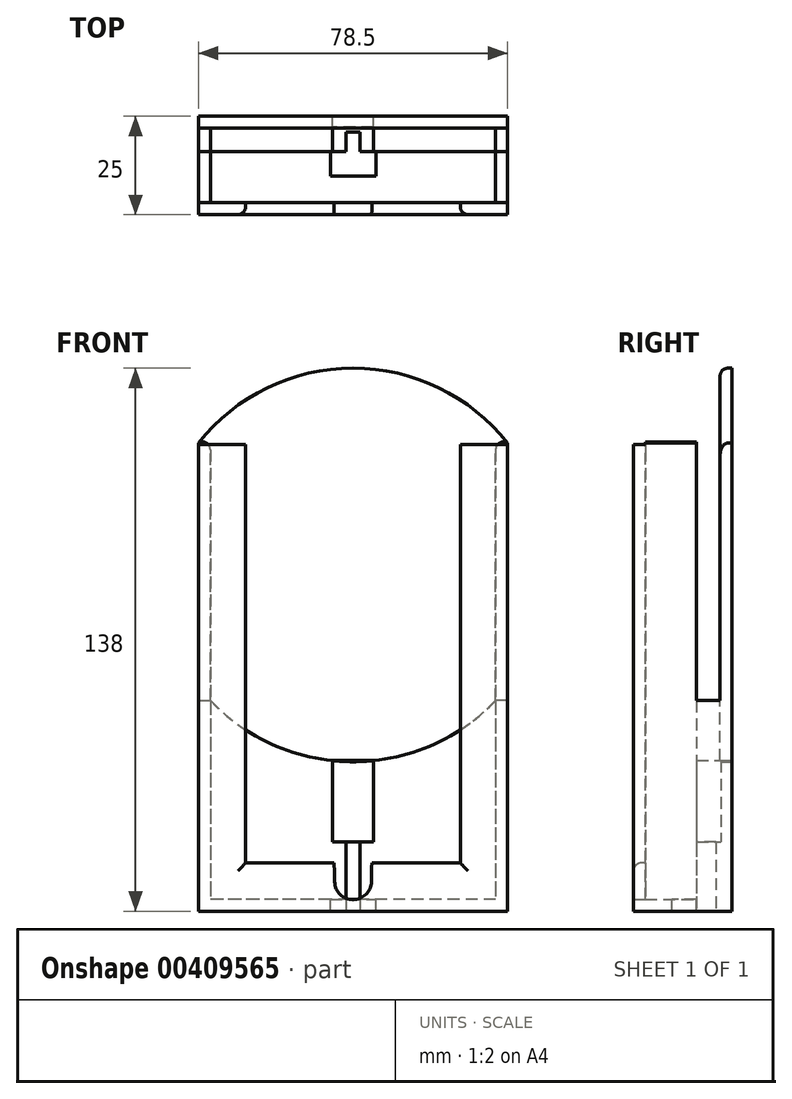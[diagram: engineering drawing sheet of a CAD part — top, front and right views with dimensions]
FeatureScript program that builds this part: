
annotation { "Feature Type Name" : "Feature", "Feature Type Description" : "" }
export const myFeature = defineFeature(function(context is Context, id is Id, definition is map)
    precondition{}
    {
        {
            var Q0;
            Q0=qCreatedBy(makeId("Front.planeOp"),FACE);
            var sketch = newSketch(context, id + "F0", { "sketchPlane" : qUnion([Q0])});
            skLineSegment(sketch, "E0.bottom", {"start": v(36.25, 70) * mm, "end": v(-36.25, 70) * mm});
            skLineSegment(sketch, "E0.top", {"start": v(36.25, -70) * mm, "end": v(-36.25, -70) * mm});
            skLineSegment(sketch, "E0.left", {"start": v(36.25, 70) * mm, "end": v(36.25, -70) * mm});
            skLineSegment(sketch, "E0.right", {"start": v(-36.25, 70) * mm, "end": v(-36.25, -70) * mm});
            skPoint(sketch, "E0.middle", {"position": v(0, 0) * mm});
            skLineSegment(sketch, "E1", {"start": v(0, -70) * mm, "end": v(0, -35) * mm, "construction": true});
            skLineSegment(sketch, "E2.bottom", {"start": v(39.25, 73) * mm, "end": v(-39.25, 73) * mm});
            skLineSegment(sketch, "E2.top", {"start": v(39.25, -73) * mm, "end": v(-39.25, -73) * mm});
            skLineSegment(sketch, "E2.left", {"start": v(39.25, 73) * mm, "end": v(39.25, -73) * mm});
            skLineSegment(sketch, "E2.right", {"start": v(-39.25, 73) * mm, "end": v(-39.25, -73) * mm});
            skLineSegment(sketch, "E3", {"start": v(-36.25, 70) * mm, "end": v(-36.25, 73) * mm});
            skLineSegment(sketch, "E4", {"start": v(36.25, 70) * mm, "end": v(36.25, 73) * mm});
            skLineSegment(sketch, "E5", {"start": v(0, -35) * mm, "end": v(0, 15) * mm, "construction": true});
            skCircle(sketch, "E6", {"center": v(0, 15) * mm, "radius": 50 * mm});
            skLineSegment(sketch, "E7", {"start": v(0, -35) * mm, "end": v(0, -55.13) * mm});
            skPoint(sketch, "E8", {"position": v(0, -55.13) * mm});
            skLineSegment(sketch, "E9", {"start": v(0, -35) * mm, "end": v(0, -45.07) * mm});
            skLineSegment(sketch, "E10.bottom", {"start": v(5.18, -34.73) * mm, "end": v(-5.18, -34.73) * mm});
            skLineSegment(sketch, "E10.top", {"start": v(5.18, -55.4) * mm, "end": v(-5.18, -55.4) * mm});
            skLineSegment(sketch, "E10.left", {"start": v(5.18, -34.73) * mm, "end": v(5.18, -55.4) * mm});
            skLineSegment(sketch, "E10.right", {"start": v(-5.18, -34.73) * mm, "end": v(-5.18, -55.4) * mm});
            skPoint(sketch, "E10.middle", {"position": v(0, -45.07) * mm});
            skSolve(sketch);
        }
        {
            var Q0;
            {var subQ0=sQuery(id+"F0.wireOp",EDGE,"E6");var subQ1=sQuery(id+"F0.wireOp",EDGE,"E0.left");var subQ2=makeQuery(id+"F0.imprint","INTERSECT",VERTEX,{"disambiguationData":[OD(0.0)],"derivedFrom":[subQ1,subQ0]});Q0=makeQuery(id+"F0.imprint","IMPRINT",FACE,{"disambiguationData":[TD([[makeQuery(id+"F0.imprint","IMPRINT",EDGE,{"disambiguationData":[TD([[subQ2,-1.0]])],"derivedFrom":subQ1}),-1.0]])]});}
            extrude(context, id + "F1", {"entities" : qUnion([Q0]), "depth" : 3 * mm});
        }
        {
            var Q0;
            {var subQ0=sQuery(id+"F0.wireOp",EDGE,"E0.top");Q0=makeQuery(id+"F0.imprint","IMPRINT",FACE,{"disambiguationData":[TD([[makeQuery(id+"F0.imprint","IMPRINT",EDGE,{"derivedFrom":subQ0}),-1.0]])]});}
            extrude(context, id + "F2", {"entities" : qUnion([Q0]), "operationType" : NewBodyOperationType.ADD, "depth" : 9 * mm});
        }
        {
            var Q0;
            {var subQ1=sQuery(id+"F0.wireOp",EDGE,"E0.top");Q0=makeQuery(id+"F0.imprint","IMPRINT",FACE,{"disambiguationData":[TD([[makeQuery(id+"F0.imprint","IMPRINT",EDGE,{"derivedFrom":subQ1}),1.0]])]});}
            extrude(context, id + "F3", {"entities" : qUnion([Q0]), "operationType" : NewBodyOperationType.ADD, "depth" : 22 * mm});
        }
        {
            var Q0;
            {var subQ0=sQuery(id+"F0.wireOp",EDGE,"E6");var subQ1=sQuery(id+"F0.wireOp",EDGE,"E0.right");var subQ2=makeQuery(id+"F0.imprint","INTERSECT",VERTEX,{"disambiguationData":[OD(0.0)],"derivedFrom":[subQ1,subQ0]});Q0=makeQuery(id+"F0.imprint","IMPRINT",FACE,{"disambiguationData":[TD([[makeQuery(id+"F0.imprint","IMPRINT",EDGE,{"disambiguationData":[TD([[subQ2,-1.0]])],"derivedFrom":subQ1}),-1.0]])]});}
            extrude(context, id + "F4", {"entities" : qUnion([Q0]), "operationType" : NewBodyOperationType.ADD, "depth" : 22 * mm});
        }
        {
            var Q0;
            {var subQ0=sQuery(id+"F0.wireOp",EDGE,"E6");var subQ1=sQuery(id+"F0.wireOp",EDGE,"E0.left");var subQ2=makeQuery(id+"F0.imprint","INTERSECT",VERTEX,{"disambiguationData":[OD(0.0)],"derivedFrom":[subQ1,subQ0]});Q0=makeQuery(id+"F0.imprint","IMPRINT",FACE,{"disambiguationData":[TD([[makeQuery(id+"F0.imprint","IMPRINT",EDGE,{"disambiguationData":[TD([[subQ2,-1.0]])],"derivedFrom":subQ1}),1.0]])]});}
            extrude(context, id + "F5", {"entities" : qUnion([Q0]), "operationType" : NewBodyOperationType.ADD, "depth" : 22 * mm});
        }
        {
            var Q0;
            {var subQ0=sQuery(id+"F0.wireOp",EDGE,"E0.right");Q0=makeQuery(id+"F4.boolean.opBoolean","MERGE",FACE,{"derivedFrom":[makeQuery(id+"F3.opExtrude","SWEPT_FACE",FACE,{"disambiguationData":[OSD([subQ0])]}),makeQuery(id+"F4.opExtrude","SWEPT_FACE",FACE,{"disambiguationData":[OSD([subQ0])]})]});}
            var sketch = newSketch(context, id + "F6", { "sketchPlane" : qUnion([Q0])});
            skLineSegment(sketch, "E11.bottom", {"start": v(-3, -19.44) * mm, "end": v(-9, -19.44) * mm});
            skLineSegment(sketch, "E11.top", {"start": v(-3, 49.44) * mm, "end": v(-9, 49.44) * mm});
            skLineSegment(sketch, "E11.left", {"start": v(-3, -19.44) * mm, "end": v(-3, 49.44) * mm});
            skLineSegment(sketch, "E11.right", {"start": v(-9, -19.44) * mm, "end": v(-9, 49.44) * mm});
            skSolve(sketch);
        }
        {
            var Q0;
            Q0=makeQuery(id+"F6.imprint","IMPRINT",FACE,{"disambiguationData":[TD([[makeQuery(id+"F6.imprint","IMPRINT",EDGE,{"derivedFrom":sQuery(id+"F6.wireOp",EDGE,"E11.bottom")}),1.0]])]});
            extrude(context, id + "F7", {"entities" : qUnion([Q0]), "operationType" : NewBodyOperationType.REMOVE, "oppositeDirection" : true, "depth" : 4 * mm});
        }
        {
            var Q0;
            {var subQ0=sQuery(id+"F0.wireOp",EDGE,"E0.left");Q0=makeQuery(id+"F5.boolean.opBoolean","MERGE",FACE,{"derivedFrom":[makeQuery(id+"F3.opExtrude","SWEPT_FACE",FACE,{"disambiguationData":[OSD([subQ0])]}),makeQuery(id+"F5.opExtrude","SWEPT_FACE",FACE,{"disambiguationData":[OSD([subQ0])]})]});}
            var sketch = newSketch(context, id + "F8", { "sketchPlane" : qUnion([Q0])});
            skLineSegment(sketch, "E12.bottom", {"start": v(3, -19.44) * mm, "end": v(9, -19.44) * mm});
            skLineSegment(sketch, "E12.top", {"start": v(3, 49.44) * mm, "end": v(9, 49.44) * mm});
            skLineSegment(sketch, "E12.left", {"start": v(3, -19.44) * mm, "end": v(3, 49.44) * mm});
            skLineSegment(sketch, "E12.right", {"start": v(9, -19.44) * mm, "end": v(9, 49.44) * mm});
            skSolve(sketch);
        }
        {
            var Q0;
            Q0=makeQuery(id+"F8.imprint","IMPRINT",FACE,{"disambiguationData":[TD([[makeQuery(id+"F8.imprint","IMPRINT",EDGE,{"derivedFrom":sQuery(id+"F8.wireOp",EDGE,"E12.bottom")}),-1.0]])]});
            extrude(context, id + "F9", {"entities" : qUnion([Q0]), "operationType" : NewBodyOperationType.REMOVE, "oppositeDirection" : true, "depth" : 4 * mm});
        }
        {
            var Q0;
            Q0=makeQuery(id+"F0.imprint","IMPRINT",FACE,{"disambiguationData":[TD([[makeQuery(id+"F0.imprint","IMPRINT",EDGE,{"derivedFrom":sQuery(id+"F0.wireOp",EDGE,"E10.top")}),-1.0]])]});
            extrude(context, id + "F10", {"entities" : qUnion([Q0]), "operationType" : NewBodyOperationType.ADD, "depth" : 2.8 * mm});
        }
        {
            var Q0;
            Q0=makeQuery(id+"F2.opExtrude","CAP_FACE",FACE,{"disambiguationData":[OSD([sQuery(id+"F0.wireOp",EDGE,"E0.top"),sQuery(id+"F0.wireOp",EDGE,"E0.left"),sQuery(id+"F0.wireOp",EDGE,"E0.right"),sQuery(id+"F0.wireOp",EDGE,"E6"),sQuery(id+"F0.wireOp",EDGE,"E10.top"),sQuery(id+"F0.wireOp",EDGE,"E10.left"),sQuery(id+"F0.wireOp",EDGE,"E10.right")])],"isStart":false});
            var sketch = newSketch(context, id + "F11", { "sketchPlane" : qUnion([Q0])});
            skLineSegment(sketch, "E13", {"start": v(0, -55.4) * mm, "end": v(0, -70) * mm, "construction": true});
            skPoint(sketch, "E14", {"position": v(0, -62.7) * mm});
            skLineSegment(sketch, "E15.bottom", {"start": v(1.75, -55.4) * mm, "end": v(-1.75, -55.4) * mm});
            skLineSegment(sketch, "E15.top", {"start": v(1.75, -70) * mm, "end": v(-1.75, -70) * mm});
            skLineSegment(sketch, "E15.left", {"start": v(1.75, -55.4) * mm, "end": v(1.75, -70) * mm});
            skLineSegment(sketch, "E15.right", {"start": v(-1.75, -55.4) * mm, "end": v(-1.75, -70) * mm});
            skSolve(sketch);
        }
        {
            var Q0;
            Q0=makeQuery(id+"F11.imprint","IMPRINT",FACE,{"disambiguationData":[TD([[makeQuery(id+"F11.imprint","IMPRINT",EDGE,{"derivedFrom":sQuery(id+"F11.wireOp",EDGE,"E15.bottom")}),1.0]])]});
            extrude(context, id + "F12", {"entities" : qUnion([Q0]), "operationType" : NewBodyOperationType.REMOVE, "oppositeDirection" : true, "depth" : 5 * mm});
        }
        {
            var Q0;
            Q0=makeQuery(id+"F12.boolean.opBoolean","MERGE",FACE,{"derivedFrom":[makeQuery(id+"F3.opExtrude","SWEPT_FACE",FACE,{"disambiguationData":[OSD([sQuery(id+"F0.wireOp",EDGE,"E0.top")])]}),makeQuery(id+"F12.opExtrude","SWEPT_FACE",FACE,{"disambiguationData":[OSD([sQuery(id+"F11.wireOp",EDGE,"E15.top")])]})]});
            var sketch = newSketch(context, id + "F13", { "sketchPlane" : qUnion([Q0])});
            skLineSegment(sketch, "E16.bottom", {"start": v(-5.73, -9) * mm, "end": v(5.9, -9) * mm});
            skLineSegment(sketch, "E16.top", {"start": v(-5.73, -15.2) * mm, "end": v(5.9, -15.2) * mm});
            skLineSegment(sketch, "E16.left", {"start": v(-5.73, -9) * mm, "end": v(-5.73, -15.2) * mm});
            skLineSegment(sketch, "E16.right", {"start": v(5.9, -9) * mm, "end": v(5.9, -15.2) * mm});
            skLineSegment(sketch, "E17.bottom", {"start": v(-1.75, -4) * mm, "end": v(1.75, -4) * mm});
            skLineSegment(sketch, "E17.top", {"start": v(-1.75, -9) * mm, "end": v(1.75, -9) * mm});
            skLineSegment(sketch, "E17.left", {"start": v(-1.75, -4) * mm, "end": v(-1.75, -9) * mm});
            skLineSegment(sketch, "E17.right", {"start": v(1.75, -4) * mm, "end": v(1.75, -9) * mm});
            skSolve(sketch);
        }
        {
            var Q0;
            Q0=makeQuery(id+"F13.imprint","IMPRINT",FACE,{"disambiguationData":[TD([[makeQuery(id+"F13.imprint","IMPRINT",EDGE,{"derivedFrom":sQuery(id+"F13.wireOp",EDGE,"E16.top")}),1.0]])]});
            extrude(context, id + "F14", {"entities" : qUnion([Q0]), "operationType" : NewBodyOperationType.REMOVE, "oppositeDirection" : true, "depth" : 4 * mm});
        }
        {
            var Q0;
            {var subQ1=sQuery(id+"F11.wireOp",EDGE,"E15.left");var subQ2=sQuery(id+"F11.wireOp",EDGE,"E15.top");var subQ3=sQuery(id+"F0.wireOp",EDGE,"E0.top");Q0=makeQuery(id+"F14.boolean.opBoolean","SPLIT",FACE,{"disambiguationData":[TD([makeQuery(id+"F12.boolean.opBoolean","COPY",FACE,{"derivedFrom":makeQuery(id+"F12.opExtrude","SWEPT_FACE",FACE,{"disambiguationData":[OSD([subQ1])]})})])],"derivedFrom":makeQuery(id+"F12.boolean.opBoolean","MERGE",FACE,{"derivedFrom":[makeQuery(id+"F3.opExtrude","SWEPT_FACE",FACE,{"disambiguationData":[OSD([subQ3])]}),makeQuery(id+"F12.opExtrude","SWEPT_FACE",FACE,{"disambiguationData":[OSD([subQ2])]})]})});}
            extrude(context, id + "F15", {"entities" : qUnion([Q0]), "operationType" : NewBodyOperationType.REMOVE, "oppositeDirection" : true, "depth" : 4 * mm});
        }
        {
            var Q0;
            {var subQ0=sQuery(id+"F0.wireOp",EDGE,"E6");var subQ1=sQuery(id+"F0.wireOp",EDGE,"E2.left");var subQ2=sQuery(id+"F0.wireOp",EDGE,"E0.left");var subQ3=sQuery(id+"F0.wireOp",EDGE,"E2.right");var subQ4=sQuery(id+"F0.wireOp",EDGE,"E0.right");Q0=makeQuery(id+"F5.boolean.opBoolean","MERGE",FACE,{"derivedFrom":[makeQuery(id+"F4.boolean.opBoolean","MERGE",FACE,{"derivedFrom":[makeQuery(id+"F3.opExtrude","CAP_FACE",FACE,{"disambiguationData":[OSD([sQuery(id+"F0.wireOp",EDGE,"E0.top"),subQ2,subQ4,sQuery(id+"F0.wireOp",EDGE,"E2.top"),subQ1,subQ3,subQ0])],"isStart":false}),makeQuery(id+"F4.opExtrude","CAP_FACE",FACE,{"disambiguationData":[OSD([subQ4,subQ3,subQ0])],"isStart":false})]}),makeQuery(id+"F5.opExtrude","CAP_FACE",FACE,{"disambiguationData":[OSD([subQ2,subQ1,subQ0])],"isStart":false})]});}
            var sketch = newSketch(context, id + "F16", { "sketchPlane" : qUnion([Q0])});
            skLineSegment(sketch, "E18.bottom", {"start": v(-39.25, -73) * mm, "end": v(-27.25, -73) * mm});
            skLineSegment(sketch, "E18.top", {"start": v(-39.25, 45.6) * mm, "end": v(-27.25, 45.6) * mm});
            skLineSegment(sketch, "E18.left", {"start": v(-39.25, -73) * mm, "end": v(-39.25, 45.6) * mm});
            skLineSegment(sketch, "E18.right", {"start": v(-27.25, -73) * mm, "end": v(-27.25, 45.6) * mm});
            skLineSegment(sketch, "E19.bottom", {"start": v(39.25, -73) * mm, "end": v(27.25, -73) * mm});
            skLineSegment(sketch, "E19.top", {"start": v(39.25, 45.6) * mm, "end": v(27.25, 45.6) * mm});
            skLineSegment(sketch, "E19.left", {"start": v(39.25, -73) * mm, "end": v(39.25, 45.6) * mm});
            skLineSegment(sketch, "E19.right", {"start": v(27.25, -73) * mm, "end": v(27.25, 45.6) * mm});
            skLineSegment(sketch, "E20.bottom", {"start": v(-27.25, -73) * mm, "end": v(27.25, -73) * mm});
            skLineSegment(sketch, "E20.top", {"start": v(-27.25, -60.7) * mm, "end": v(27.25, -60.7) * mm});
            skLineSegment(sketch, "E20.left", {"start": v(-27.25, -73) * mm, "end": v(-27.25, -60.7) * mm});
            skLineSegment(sketch, "E20.right", {"start": v(27.25, -73) * mm, "end": v(27.25, -60.7) * mm});
            skSolve(sketch);
        }
        {
            var Q0;
            Q0 = qSketchRegion(id + "F16", true);
            extrude(context, id + "F17", {"entities" : qUnion([Q0]), "operationType" : NewBodyOperationType.ADD, "depth" : 3 * mm});
        }
        {
            var Q0;
            Q0=makeQuery(id+"F17.opExtrude","CAP_FACE",FACE,{"disambiguationData":[OSD([sQuery(id+"F16.wireOp",EDGE,"E18.bottom"),sQuery(id+"F16.wireOp",EDGE,"E18.top"),sQuery(id+"F16.wireOp",EDGE,"E18.left"),sQuery(id+"F16.wireOp",EDGE,"E18.right"),sQuery(id+"F16.wireOp",EDGE,"E19.bottom"),sQuery(id+"F16.wireOp",EDGE,"E19.top"),sQuery(id+"F16.wireOp",EDGE,"E19.left"),sQuery(id+"F16.wireOp",EDGE,"E19.right"),sQuery(id+"F16.wireOp",EDGE,"E20.bottom"),sQuery(id+"F16.wireOp",EDGE,"E20.top")])],"isStart":false});
            var sketch = newSketch(context, id + "F18", { "sketchPlane" : qUnion([Q0])});
            skCircle(sketch, "E21", {"center": v(0, -65.38) * mm, "radius": 4.67 * mm});
            skLineSegment(sketch, "E22", {"start": v(-4.67, -65.5) * mm, "end": v(-4.8, -60.7) * mm});
            skLineSegment(sketch, "E23", {"start": v(-4.8, -60.7) * mm, "end": v(4.78, -60.7) * mm});
            skLineSegment(sketch, "E24", {"start": v(4.78, -60.7) * mm, "end": v(4.68, -65.48) * mm});
            skSolve(sketch);
        }
        {
            var Q0;
            {var subQ0=sQuery(id+"F18.wireOp",EDGE,"E21");var subQ1=makeQuery(id+"F18.imprint","INTERSECT",VERTEX,{"derivedFrom":[subQ0,sQuery(id+"F18.wireOp",EDGE,"E22")]});Q0=makeQuery(id+"F18.imprint","IMPRINT",FACE,{"disambiguationData":[TD([[makeQuery(id+"F18.imprint","IMPRINT",EDGE,{"disambiguationData":[TD([[subQ1,1.0]])],"derivedFrom":subQ0}),1.0]])]});}
            var Q1;
            {var subQ0=sQuery(id+"F18.wireOp",EDGE,"E24");Q1=makeQuery(id+"F18.imprint","IMPRINT",FACE,{"disambiguationData":[TD([[makeQuery(id+"F18.imprint","IMPRINT",EDGE,{"derivedFrom":subQ0}),-1.0]])]});}
            var Q2;
            {var subQ0=sQuery(id+"F18.wireOp",EDGE,"E22");Q2=makeQuery(id+"F18.imprint","IMPRINT",FACE,{"disambiguationData":[TD([[makeQuery(id+"F18.imprint","IMPRINT",EDGE,{"derivedFrom":subQ0}),-1.0]])]});}
            extrude(context, id + "F19", {"entities" : qUnion([Q0, Q1, Q2]), "operationType" : NewBodyOperationType.REMOVE, "oppositeDirection" : true, "depth" : 3 * mm});
        }
        {
            var Q0;
            Q0=makeQuery(id+"F17.opExtrude","CAP_EDGE",EDGE,{"disambiguationData":[OSD([sQuery(id+"F16.wireOp",EDGE,"E18.right")])],"isStart":false});
            var Q1;
            Q1=makeQuery(id+"F17.opExtrude","CAP_EDGE",EDGE,{"disambiguationData":[OSD([sQuery(id+"F16.wireOp",EDGE,"E19.right")])],"isStart":false});
            var Q2;
            {var subQ0=sQuery(id+"F16.wireOp",EDGE,"E20.top");var subQ1=sQuery(id+"F16.wireOp",EDGE,"E19.right");Q2=makeQuery(id+"F19.boolean.opBoolean","SPLIT",EDGE,{"disambiguationData":[TD([makeQuery(id+"F17.opExtrude","SWEPT_FACE",FACE,{"disambiguationData":[OSD([subQ1])]})])],"derivedFrom":makeQuery(id+"F17.opExtrude","CAP_EDGE",EDGE,{"disambiguationData":[OSD([subQ0])],"isStart":false})});}
            var Q3;
            {var subQ0=sQuery(id+"F16.wireOp",EDGE,"E20.top");var subQ1=sQuery(id+"F16.wireOp",EDGE,"E18.right");Q3=makeQuery(id+"F19.boolean.opBoolean","SPLIT",EDGE,{"disambiguationData":[TD([makeQuery(id+"F17.opExtrude","SWEPT_FACE",FACE,{"disambiguationData":[OSD([subQ1])]})])],"derivedFrom":makeQuery(id+"F17.opExtrude","CAP_EDGE",EDGE,{"disambiguationData":[OSD([subQ0])],"isStart":false})});}
            var Q4;
            Q4=makeQuery(id+"F19.boolean.opBoolean","COPY",EDGE,{"derivedFrom":makeQuery(id+"F19.opExtrude","CAP_EDGE",EDGE,{"disambiguationData":[OSD([sQuery(id+"F18.wireOp",EDGE,"E22")])],"isStart":true})});
            var Q5;
            {var subQ0=sQuery(id+"F0.wireOp",EDGE,"E6");var subQ1=sQuery(id+"F0.wireOp",EDGE,"E2.right");var subQ4=sQuery(id+"F0.wireOp",EDGE,"E0.left");var subQ5=sQuery(id+"F0.wireOp",EDGE,"E2.left");var subQ8=makeQuery(id+"F0.imprint","INTERSECT",VERTEX,{"disambiguationData":[OD(0.0)],"derivedFrom":[subQ4,subQ0]});Q5=makeQuery(id+"F9.boolean.opBoolean","INTERSECT",EDGE,{"derivedFrom":[makeQuery(id+"F7.boolean.opBoolean","SPLIT",FACE,{"disambiguationData":[TD([makeQuery(id+"F3.opExtrude","SWEPT_FACE",FACE,{"disambiguationData":[OSD([subQ4])]})])],"derivedFrom":makeQuery(id+"F5.boolean.opBoolean","MERGE",FACE,{"derivedFrom":[makeQuery(id+"F4.boolean.opBoolean","MERGE",FACE,{"derivedFrom":[makeQuery(id+"F1.opExtrude","SWEPT_FACE",FACE,{"disambiguationData":[OSD([subQ0]),TDD([makeQuery(id+"F0.imprint","IMPRINT",EDGE,{"disambiguationData":[TD([[subQ8,-1.0]])],"derivedFrom":subQ0})])]}),makeQuery(id+"F4.opExtrude","SWEPT_FACE",FACE,{"disambiguationData":[OSD([subQ0]),TDD([makeQuery(id+"F0.imprint","IMPRINT",EDGE,{"disambiguationData":[TD([[makeQuery(id+"F0.imprint","INTERSECT",VERTEX,{"disambiguationData":[OD(0.0)],"derivedFrom":[subQ1,subQ0]}),1.0]])],"derivedFrom":subQ0})])]})]}),makeQuery(id+"F5.opExtrude","SWEPT_FACE",FACE,{"disambiguationData":[OSD([subQ0]),TDD([makeQuery(id+"F0.imprint","IMPRINT",EDGE,{"disambiguationData":[TD([[makeQuery(id+"F0.imprint","INTERSECT",VERTEX,{"disambiguationData":[OD(0.0)],"derivedFrom":[subQ5,subQ0]}),-1.0]])],"derivedFrom":subQ0})])]})]})}),makeQuery(id+"F9.opExtrude","SWEPT_FACE",FACE,{"disambiguationData":[OSD([sQuery(id+"F8.wireOp",EDGE,"E12.left")])]})]});}
            var Q6;
            {var subQ0=sQuery(id+"F0.wireOp",EDGE,"E6");var subQ1=sQuery(id+"F0.wireOp",EDGE,"E0.left");Q6=makeQuery(id+"F5.opExtrude","SWEPT_EDGE",EDGE,{"disambiguationData":[OSD([subQ1,subQ0]),TDD([makeQuery(id+"F0.imprint","INTERSECT",VERTEX,{"disambiguationData":[OD(0.0)],"derivedFrom":[subQ1,subQ0]})])]});}
            var Q7;
            {var subQ0=sQuery(id+"F0.wireOp",EDGE,"E6");var subQ1=sQuery(id+"F0.wireOp",EDGE,"E0.right");Q7=makeQuery(id+"F4.opExtrude","SWEPT_EDGE",EDGE,{"disambiguationData":[OSD([subQ1,subQ0]),TDD([makeQuery(id+"F0.imprint","INTERSECT",VERTEX,{"disambiguationData":[OD(0.0)],"derivedFrom":[subQ1,subQ0]})])]});}
            fillet(context, id + "F20", {"entities" : qUnion([Q0, Q1, Q2, Q3, Q4, Q5, Q6, Q7]), "radius" : 2 * mm, "tangentPropagation" : true, "allowEdgeOverflow" : false});
        }
    });
